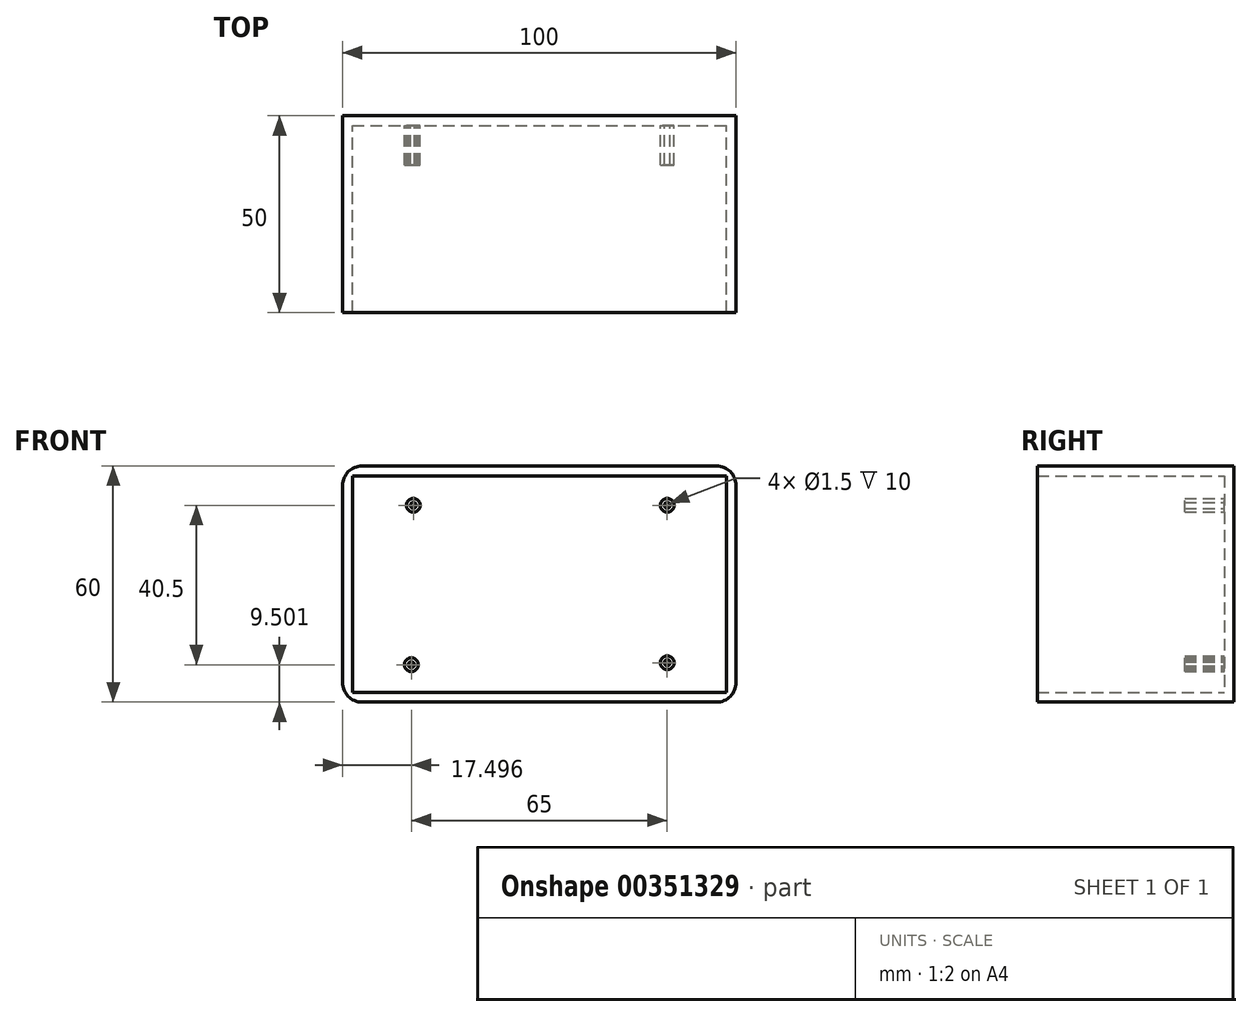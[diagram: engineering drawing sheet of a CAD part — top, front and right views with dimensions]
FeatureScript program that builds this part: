
annotation { "Feature Type Name" : "Feature", "Feature Type Description" : "" }
export const myFeature = defineFeature(function(context is Context, id is Id, definition is map)
    precondition{}
    {
        {
            var Q0;
            Q0=qCreatedBy(makeId("Front.planeOp"),FACE);
            var sketch = newSketch(context, id + "F0", { "sketchPlane" : qUnion([Q0])});
            skLineSegment(sketch, "E0.bottom", {"start": v(-114.08, 48.25) * mm, "end": v(-14.08, 48.25) * mm});
            skLineSegment(sketch, "E0.top", {"start": v(-114.08, -11.75) * mm, "end": v(-14.08, -11.75) * mm});
            skLineSegment(sketch, "E0.left", {"start": v(-114.08, 48.25) * mm, "end": v(-114.08, -11.75) * mm});
            skLineSegment(sketch, "E0.right", {"start": v(-14.08, 48.25) * mm, "end": v(-14.08, -11.75) * mm});
            skSolve(sketch);
        }
        {
            var Q0;
            Q0=makeQuery(id+"F0.imprint","IMPRINT",FACE,{"disambiguationData":[TD([[makeQuery(id+"F0.imprint","IMPRINT",EDGE,{"derivedFrom":sQuery(id+"F0.wireOp",EDGE,"E0.bottom")}),-1.0]])]});
            extrude(context, id + "F1", {"entities" : qUnion([Q0]), "depth" : 50 * mm});
        }
        {
            var Q0;
            Q0=makeQuery(id+"F1.opExtrude","CAP_FACE",FACE,{"disambiguationData":[OSD([sQuery(id+"F0.wireOp",EDGE,"E0.bottom"),sQuery(id+"F0.wireOp",EDGE,"E0.top"),sQuery(id+"F0.wireOp",EDGE,"E0.left"),sQuery(id+"F0.wireOp",EDGE,"E0.right")])],"isStart":false});
            shell(context, id + "F2", {"entities" : qUnion([Q0]), "thickness" : 2.5 * mm});
        }
        {
            var Q0;
            Q0=makeQuery(id+"F2.opShell","OFFSET_FACE",FACE,{"disambiguationData":[OSD([sQuery(id+"F0.wireOp",EDGE,"E0.bottom"),sQuery(id+"F0.wireOp",EDGE,"E0.top"),sQuery(id+"F0.wireOp",EDGE,"E0.left"),sQuery(id+"F0.wireOp",EDGE,"E0.right")])]});
            var sketch = newSketch(context, id + "F3", { "sketchPlane" : qUnion([Q0])});
            skCircle(sketch, "E1", {"center": v(-96.08, 38.25) * mm, "radius": 1.75 * mm});
            skCircle(sketch, "E2", {"center": v(-31.58, 38.25) * mm, "radius": 1.75 * mm});
            skCircle(sketch, "E3", {"center": v(-96.58, -2.25) * mm, "radius": 1.75 * mm});
            skCircle(sketch, "E4", {"center": v(-31.58, -1.75) * mm, "radius": 1.75 * mm});
            skCircle(sketch, "E5.0", {"center": v(-96.08, 38.25) * mm, "radius": 0.75 * mm});
            skCircle(sketch, "E6.0", {"center": v(-31.58, 38.25) * mm, "radius": 0.75 * mm});
            skCircle(sketch, "E7.0", {"center": v(-96.58, -2.25) * mm, "radius": 0.75 * mm});
            skCircle(sketch, "E8.0", {"center": v(-31.58, -1.75) * mm, "radius": 0.75 * mm});
            skSolve(sketch);
        }
        {
            var Q0;
            Q0 = qSketchRegion(id + "F3", true);
            extrude(context, id + "F4", {"entities" : qUnion([Q0]), "operationType" : NewBodyOperationType.ADD, "depth" : 10 * mm});
        }
        {
            var Q0;
            Q0=makeQuery(id+"F1.opExtrude","SWEPT_EDGE",EDGE,{"disambiguationData":[OSD([sQuery(id+"F0.wireOp",EDGE,"E0.bottom"),sQuery(id+"F0.wireOp",EDGE,"E0.left")])]});
            var Q1;
            Q1=makeQuery(id+"F1.opExtrude","SWEPT_EDGE",EDGE,{"disambiguationData":[OSD([sQuery(id+"F0.wireOp",EDGE,"E0.top"),sQuery(id+"F0.wireOp",EDGE,"E0.left")])]});
            var Q2;
            Q2=makeQuery(id+"F1.opExtrude","SWEPT_EDGE",EDGE,{"disambiguationData":[OSD([sQuery(id+"F0.wireOp",EDGE,"E0.top"),sQuery(id+"F0.wireOp",EDGE,"E0.right")])]});
            var Q3;
            Q3=makeQuery(id+"F1.opExtrude","SWEPT_EDGE",EDGE,{"disambiguationData":[OSD([sQuery(id+"F0.wireOp",EDGE,"E0.bottom"),sQuery(id+"F0.wireOp",EDGE,"E0.right")])]});
            fillet(context, id + "F5", {"entities" : qUnion([Q0, Q1, Q2, Q3]), "radius" : 5 * mm, "tangentPropagation" : true, "allowEdgeOverflow" : false});
        }
    });
